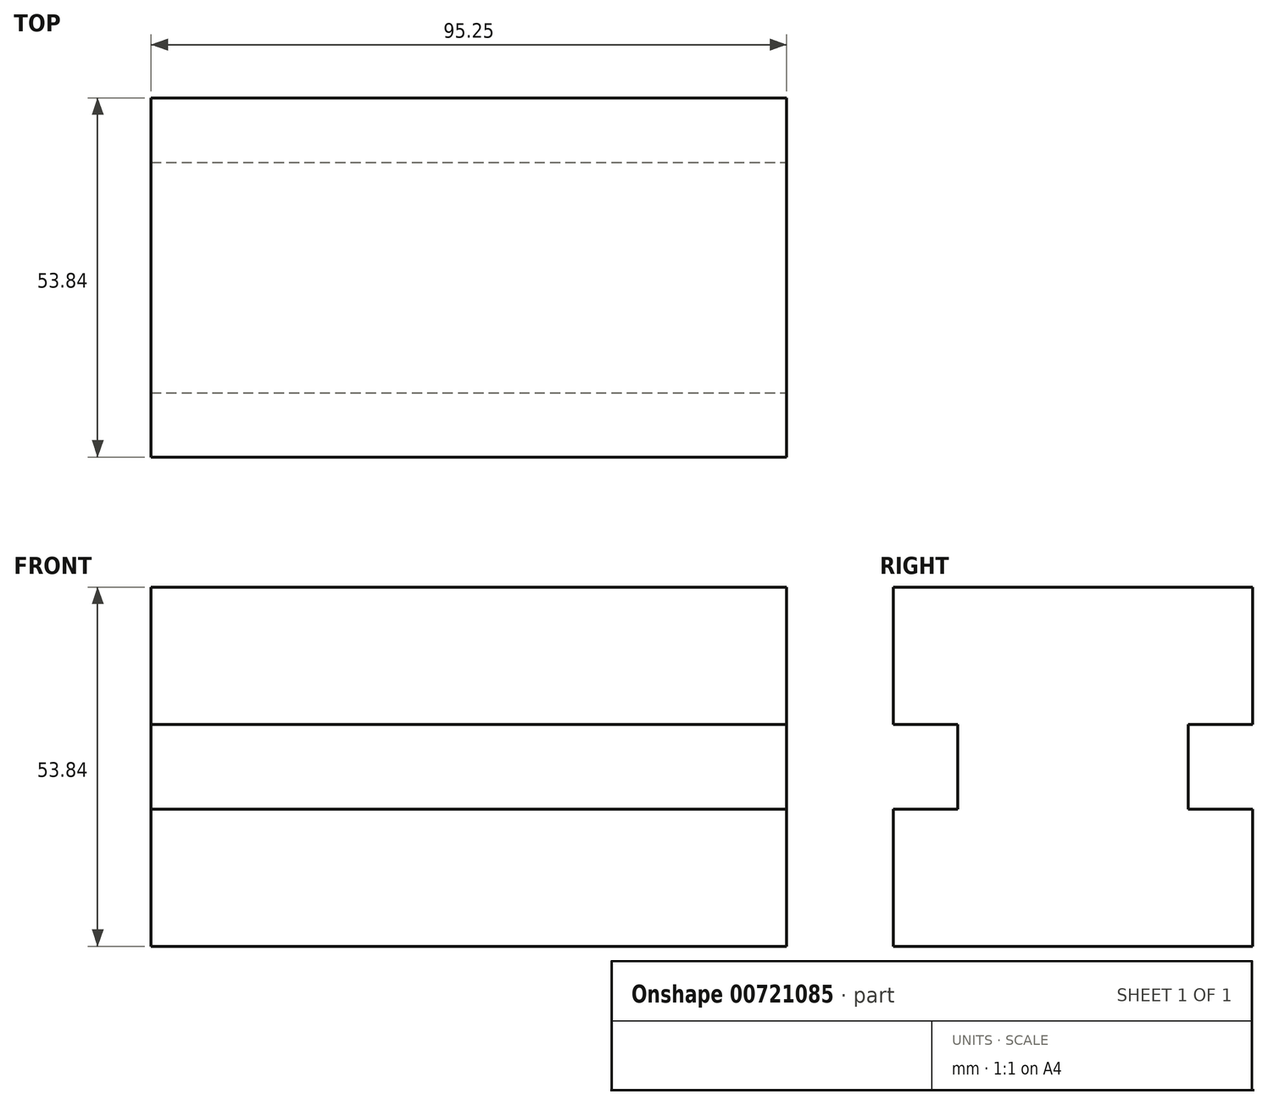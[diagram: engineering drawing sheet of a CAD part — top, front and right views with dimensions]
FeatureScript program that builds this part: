
annotation { "Feature Type Name" : "Feature", "Feature Type Description" : "" }
export const myFeature = defineFeature(function(context is Context, id is Id, definition is map)
    precondition{}
    {
        {
            var Q0;
            Q0=qCreatedBy(makeId("Right.planeOp"),FACE);
            var sketch = newSketch(context, id + "F0", { "sketchPlane" : qUnion([Q0])});
            skLineSegment(sketch, "E0.bottom", {"start": v(26.92, -26.92) * mm, "end": v(-26.92, -26.92) * mm});
            skLineSegment(sketch, "E0.top", {"start": v(26.92, 26.92) * mm, "end": v(-26.92, 26.92) * mm});
            skLineSegment(sketch, "E0.left", {"start": v(26.92, -26.92) * mm, "end": v(26.92, -6.35) * mm});
            skLineSegment(sketch, "E0.right", {"start": v(-26.92, -26.92) * mm, "end": v(-26.92, -6.35) * mm});
            skPoint(sketch, "E0.middle", {"position": v(0, 0) * mm});
            skLineSegment(sketch, "E1.bottom", {"start": v(-26.92, 6.35) * mm, "end": v(-17.27, 6.35) * mm});
            skLineSegment(sketch, "E1.top", {"start": v(-26.92, -6.35) * mm, "end": v(-17.27, -6.35) * mm});
            skLineSegment(sketch, "E1.right", {"start": v(-17.27, 6.35) * mm, "end": v(-17.27, -6.35) * mm});
            skLineSegment(sketch, "E2", {"start": v(0, 47.8) * mm, "end": v(0, -50.12) * mm, "construction": true});
            skPoint(sketch, "E2.startSnap0", {"position": v(0, 26.92) * mm});
            skLineSegment(sketch, "E3.MirrorCS", {"start": v(26.92, 6.35) * mm, "end": v(17.27, 6.35) * mm});
            skLineSegment(sketch, "E4.MirrorCS", {"start": v(17.27, 6.35) * mm, "end": v(17.27, -6.35) * mm});
            skLineSegment(sketch, "E5.MirrorCS", {"start": v(26.92, -6.35) * mm, "end": v(17.27, -6.35) * mm});
            skLineSegment(sketch, "E6.trimOffspring", {"start": v(-26.92, 6.35) * mm, "end": v(-26.92, 26.92) * mm});
            skLineSegment(sketch, "E7.trimOffspring", {"start": v(26.92, 6.35) * mm, "end": v(26.92, 26.92) * mm});
            skSolve(sketch);
        }
        {
            var Q0;
            Q0=makeQuery(id+"F0.imprint","IMPRINT",FACE,{"disambiguationData":[TD([[makeQuery(id+"F0.imprint","IMPRINT",EDGE,{"derivedFrom":sQuery(id+"F0.wireOp",EDGE,"E0.bottom")}),-1.0]])]});
            extrude(context, id + "F1", {"entities" : qUnion([Q0]), "oppositeDirection" : true, "depth" : 95.25 * mm, "offsetDistance" : 25.4 * mm});
        }
    });
